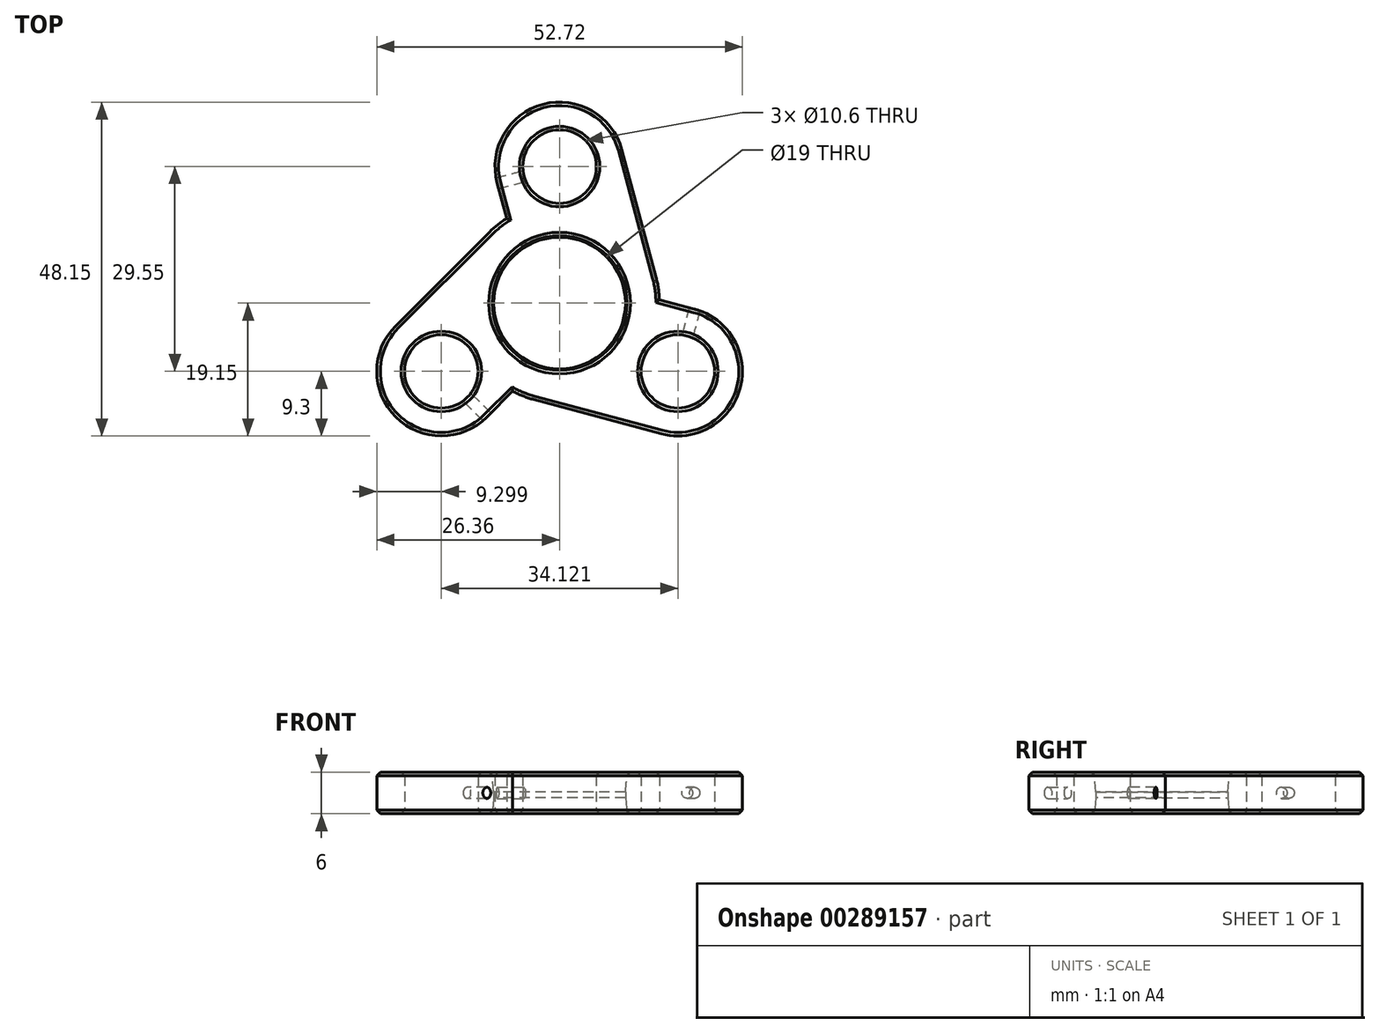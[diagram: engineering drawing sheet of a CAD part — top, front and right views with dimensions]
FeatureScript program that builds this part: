
annotation { "Feature Type Name" : "Feature", "Feature Type Description" : "" }
export const myFeature = defineFeature(function(context is Context, id is Id, definition is map)
    precondition{}
    {
        {
            var Q0;
            Q0=qCreatedBy(makeId("Top.planeOp"),FACE);
            var sketch = newSketch(context, id + "F0", { "sketchPlane" : qUnion([Q0])});
            skCircle(sketch, "E0", {"center": v(0, 19.7) * mm, "radius": 5.3 * mm});
            skCircle(sketch, "E1.1.0", {"center": v(-17.06, -9.85) * mm, "radius": 5.3 * mm});
            skCircle(sketch, "E1.2.0", {"center": v(17.06, -9.85) * mm, "radius": 5.3 * mm});
            skPoint(sketch, "E1.center", {"position": v(0, 0) * mm});
            skCircle(sketch, "E2", {"center": v(0, 0) * mm, "radius": 25 * mm, "construction": true});
            skCircle(sketch, "E3", {"center": v(0, 0) * mm, "radius": 9.5 * mm});
            skCircle(sketch, "E4", {"center": v(0, 0) * mm, "radius": 14.4 * mm});
            skArc(sketch, "E5", {"start": v(8.98, 22.1) * mm, "mid": v(-2.4, 28.68) * mm, "end": v(-8.98, 17.3) * mm});
            skLineSegment(sketch, "E6", {"start": v(8.98, 22.1) * mm, "end": v(13.9, 3.73) * mm});
            skLineSegment(sketch, "E7", {"start": v(8.98, 22.1) * mm, "end": v(-8.98, 17.3) * mm, "construction": true});
            skLineSegment(sketch, "E8", {"start": v(-8.98, 17.3) * mm, "end": v(-7.62, 12.22) * mm});
            skArc(sketch, "E9.1.0", {"start": v(-23.64, -3.27) * mm, "mid": v(-23.64, -16.43) * mm, "end": v(-10.48, -16.43) * mm});
            skLineSegment(sketch, "E9.1.1", {"start": v(-10.48, -16.43) * mm, "end": v(-6.77, -12.7) * mm});
            skLineSegment(sketch, "E9.1.2", {"start": v(-23.64, -3.27) * mm, "end": v(-10.18, 10.18) * mm});
            skArc(sketch, "E9.2.0", {"start": v(14.65, -18.83) * mm, "mid": v(26.04, -12.26) * mm, "end": v(19.47, -0.87) * mm});
            skLineSegment(sketch, "E9.2.1", {"start": v(19.47, -0.87) * mm, "end": v(14.4, 0.5) * mm});
            skLineSegment(sketch, "E9.2.2", {"start": v(14.65, -18.83) * mm, "end": v(-3.73, -13.9) * mm});
            skSolve(sketch);
        }
        {
            var Q0;
            Q0=makeQuery(id+"F0.imprint","IMPRINT",FACE,{"disambiguationData":[TD([[makeQuery(id+"F0.imprint","IMPRINT",EDGE,{"derivedFrom":sQuery(id+"F0.wireOp",EDGE,"E3")}),-1.0]])]});
            var Q1;
            {var subQ2=sQuery(id+"F0.wireOp",EDGE,"E0");Q1=makeQuery(id+"F0.imprint","IMPRINT",FACE,{"disambiguationData":[TD([[makeQuery(id+"F0.imprint","IMPRINT",EDGE,{"derivedFrom":subQ2}),-1.0]])]});}
            var Q2;
            {var subQ2=sQuery(id+"F0.wireOp",EDGE,"E1.2.0");Q2=makeQuery(id+"F0.imprint","IMPRINT",FACE,{"disambiguationData":[TD([[makeQuery(id+"F0.imprint","IMPRINT",EDGE,{"derivedFrom":subQ2}),-1.0]])]});}
            var Q3;
            {var subQ2=sQuery(id+"F0.wireOp",EDGE,"E1.1.0");Q3=makeQuery(id+"F0.imprint","IMPRINT",FACE,{"disambiguationData":[TD([[makeQuery(id+"F0.imprint","IMPRINT",EDGE,{"derivedFrom":subQ2}),-1.0]])]});}
            extrude(context, id + "F1", {"entities" : qUnion([Q0, Q1, Q2, Q3]), "depth" : 6 * mm});
        }
        {
            var Q0;
            Q0=makeQuery(id+"F1.opExtrude","CAP_EDGE",EDGE,{"disambiguationData":[OSD([sQuery(id+"F0.wireOp",EDGE,"E3")])],"isStart":true});
            chamfer(context, id + "F2", {"entities" : qUnion([Q0]), "chamferType" : ChamferType.OFFSET_ANGLE, "width" : 0.2 * mm, "oppositeDirection" : false, "angle" : 85 * degree, "tangentPropagation" : true});
        }
        {
            var Q0;
            Q0=makeQuery(id+"F1.opExtrude","CAP_EDGE",EDGE,{"disambiguationData":[OSD([sQuery(id+"F0.wireOp",EDGE,"E3")])],"isStart":false});
            chamfer(context, id + "F3", {"entities" : qUnion([Q0]), "chamferType" : ChamferType.OFFSET_ANGLE, "width" : 2.85 * mm, "oppositeDirection" : false, "angle" : 5 * degree, "tangentPropagation" : true});
        }
        {
            var Q0;
            Q0=makeQuery(id+"F1.opExtrude","CAP_FACE",FACE,{"disambiguationData":[OSD([sQuery(id+"F0.wireOp",EDGE,"E0"),sQuery(id+"F0.wireOp",EDGE,"E1.1.0"),sQuery(id+"F0.wireOp",EDGE,"E1.2.0"),sQuery(id+"F0.wireOp",EDGE,"E3"),sQuery(id+"F0.wireOp",EDGE,"E4"),sQuery(id+"F0.wireOp",EDGE,"E5"),sQuery(id+"F0.wireOp",EDGE,"E6"),sQuery(id+"F0.wireOp",EDGE,"E8"),sQuery(id+"F0.wireOp",EDGE,"E9.1.0"),sQuery(id+"F0.wireOp",EDGE,"E9.1.1"),sQuery(id+"F0.wireOp",EDGE,"E9.1.2"),sQuery(id+"F0.wireOp",EDGE,"E9.2.0"),sQuery(id+"F0.wireOp",EDGE,"E9.2.1"),sQuery(id+"F0.wireOp",EDGE,"E9.2.2")])],"isStart":false});
            var Q1;
            Q1=makeQuery(id+"F1.opExtrude","CAP_FACE",FACE,{"disambiguationData":[OSD([sQuery(id+"F0.wireOp",EDGE,"E0"),sQuery(id+"F0.wireOp",EDGE,"E1.1.0"),sQuery(id+"F0.wireOp",EDGE,"E1.2.0"),sQuery(id+"F0.wireOp",EDGE,"E3"),sQuery(id+"F0.wireOp",EDGE,"E4"),sQuery(id+"F0.wireOp",EDGE,"E5"),sQuery(id+"F0.wireOp",EDGE,"E6"),sQuery(id+"F0.wireOp",EDGE,"E8"),sQuery(id+"F0.wireOp",EDGE,"E9.1.0"),sQuery(id+"F0.wireOp",EDGE,"E9.1.1"),sQuery(id+"F0.wireOp",EDGE,"E9.1.2"),sQuery(id+"F0.wireOp",EDGE,"E9.2.0"),sQuery(id+"F0.wireOp",EDGE,"E9.2.1"),sQuery(id+"F0.wireOp",EDGE,"E9.2.2")])],"isStart":true});
            chamfer(context, id + "F4", {"entities" : qUnion([Q0, Q1]), "width" : 0.5 * mm, "tangentPropagation" : true});
        }
        {
            var Q0;
            Q0=makeQuery(id+"F1.opExtrude","SWEPT_FACE",FACE,{"disambiguationData":[OSD([sQuery(id+"F0.wireOp",EDGE,"E9.1.1")])]});
            var sketch = newSketch(context, id + "F5", { "sketchPlane" : qUnion([Q0])});
            skCircle(sketch, "E10", {"center": v(-19.03, 3) * mm, "radius": 0.8 * mm});
            skSolve(sketch);
        }
        {
            var Q0;
            {var subQ0=sQuery(id+"F5.wireOp",EDGE,"E10");var subQ1=makeQuery(id+"F1.opExtrude","SWEPT_EDGE",EDGE,{"disambiguationData":[OSD([sQuery(id+"F0.wireOp",EDGE,"E9.1.0"),sQuery(id+"F0.wireOp",EDGE,"E9.1.1")])]});var subQ2=makeQuery(id+"F5.imprint","INTERSECT",VERTEX,{"disambiguationData":[OD(0.0)],"derivedFrom":[subQ1,subQ0]});Q0=makeQuery(id+"F5.imprint","IMPRINT",FACE,{"disambiguationData":[TD([[makeQuery(id+"F5.imprint","IMPRINT",EDGE,{"disambiguationData":[TD([[subQ2,-1.0]])],"derivedFrom":subQ0}),1.0]])]});}
            var Q1;
            {var subQ0=sQuery(id+"F5.wireOp",EDGE,"E10");var subQ1=makeQuery(id+"F1.opExtrude","SWEPT_EDGE",EDGE,{"disambiguationData":[OSD([sQuery(id+"F0.wireOp",EDGE,"E9.1.0"),sQuery(id+"F0.wireOp",EDGE,"E9.1.1")])]});var subQ2=makeQuery(id+"F5.imprint","INTERSECT",VERTEX,{"disambiguationData":[OD(0.0)],"derivedFrom":[subQ1,subQ0]});Q1=makeQuery(id+"F5.imprint","IMPRINT",FACE,{"disambiguationData":[TD([[makeQuery(id+"F5.imprint","IMPRINT",EDGE,{"disambiguationData":[TD([[subQ2,1.0]])],"derivedFrom":subQ0}),1.0]])]});}
            extrude(context, id + "F6", {"entities" : qUnion([Q0, Q1]), "endBound" : BoundingType.SYMMETRIC, "depth" : 25 * mm});
        }
        {
            var Q0;
            Q0=qCreatedBy(makeId("Front.planeOp"),FACE);
            var sketch = newSketch(context, id + "F7", { "sketchPlane" : qUnion([Q0])});
            skLineSegment(sketch, "E11", {"start": v(0, 11.1) * mm, "end": v(0, -12.06) * mm});
            skSolve(sketch);
        }
        {
            var Q0;
            Q0=makeQuery(id+"F6.opExtrude","SWEPT_BODY",BODY,{"disambiguationData":[OSD([sQuery(id+"F5.wireOp",EDGE,"E10")])]});
            var Q1;
            Q1=sQuery(id+"F7.wireOp",EDGE,"E11");
            circularPattern(context, id + "F8", {"operationType" : NewBodyOperationType.REMOVE, "entities" : qUnion([Q0]), "axis" : qUnion([Q1]), "angle" : 360 * degree, "instanceCount" : 3, "equalSpace" : true});
        }
    });
